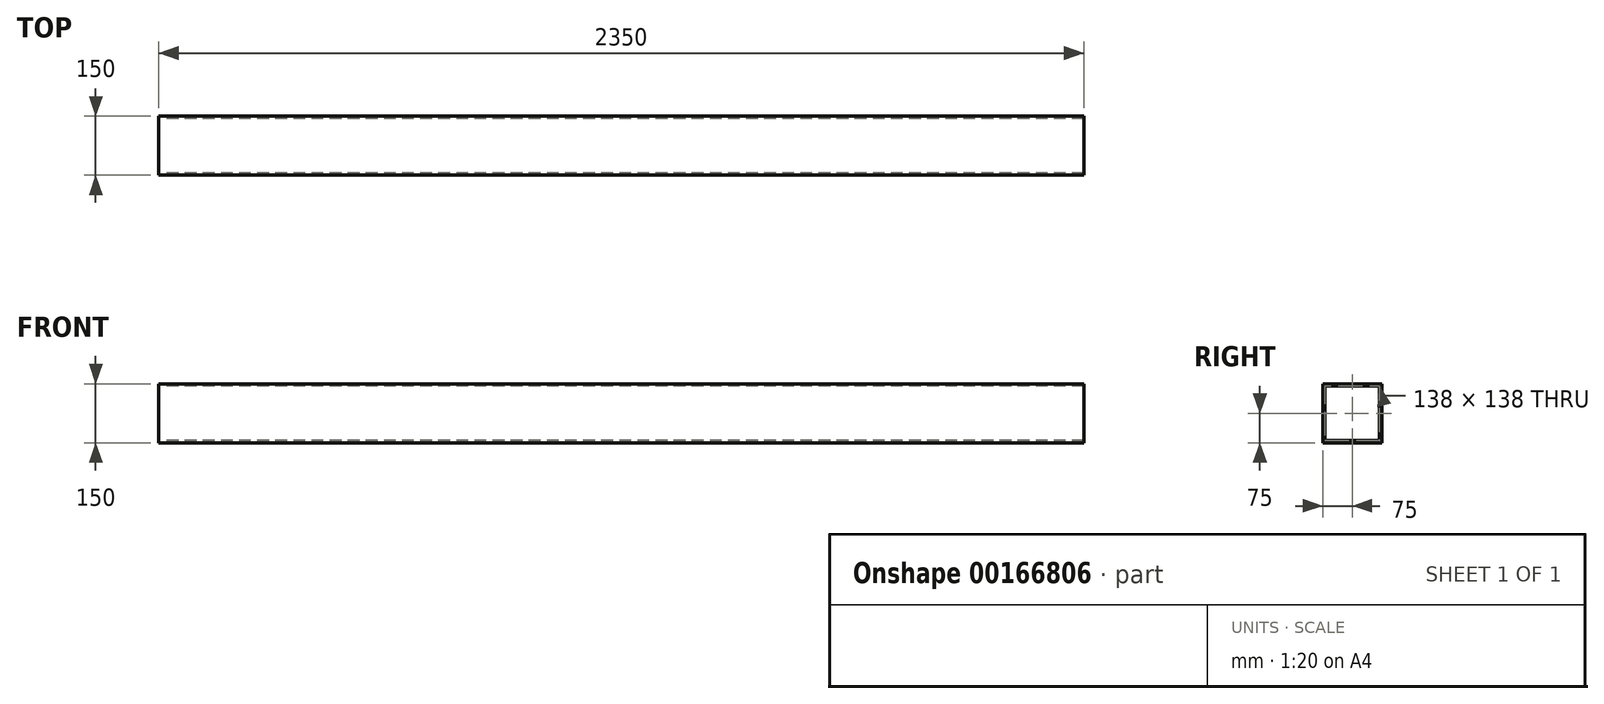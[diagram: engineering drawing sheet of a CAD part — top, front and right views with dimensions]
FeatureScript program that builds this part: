
annotation { "Feature Type Name" : "Feature", "Feature Type Description" : "" }
export const myFeature = defineFeature(function(context is Context, id is Id, definition is map)
    precondition{}
    {
        {
            var Q0;
            Q0=qCreatedBy(makeId("Right.planeOp"),FACE);
            var sketch = newSketch(context, id + "F0", { "sketchPlane" : qUnion([Q0])});
            skLineSegment(sketch, "E0.bottom", {"start": v(0, 0) * mm, "end": v(150, 0) * mm});
            skLineSegment(sketch, "E0.top", {"start": v(0, 150) * mm, "end": v(150, 150) * mm});
            skLineSegment(sketch, "E0.left", {"start": v(0, 0) * mm, "end": v(0, 150) * mm});
            skLineSegment(sketch, "E0.right", {"start": v(150, 0) * mm, "end": v(150, 150) * mm});
            skLineSegment(sketch, "E1.0", {"start": v(6, 6) * mm, "end": v(6, 144) * mm});
            skLineSegment(sketch, "E1.1", {"start": v(6, 6) * mm, "end": v(144, 6) * mm});
            skLineSegment(sketch, "E1.2", {"start": v(144, 6) * mm, "end": v(144, 144) * mm});
            skLineSegment(sketch, "E1.3", {"start": v(6, 144) * mm, "end": v(144, 144) * mm});
            skSolve(sketch);
        }
        {
            var Q0;
            Q0 = qSketchRegion(id + "F0", true);
            extrude(context, id + "F1", {"entities" : qUnion([Q0]), "depth" : 2350 * mm});
        }
    });
